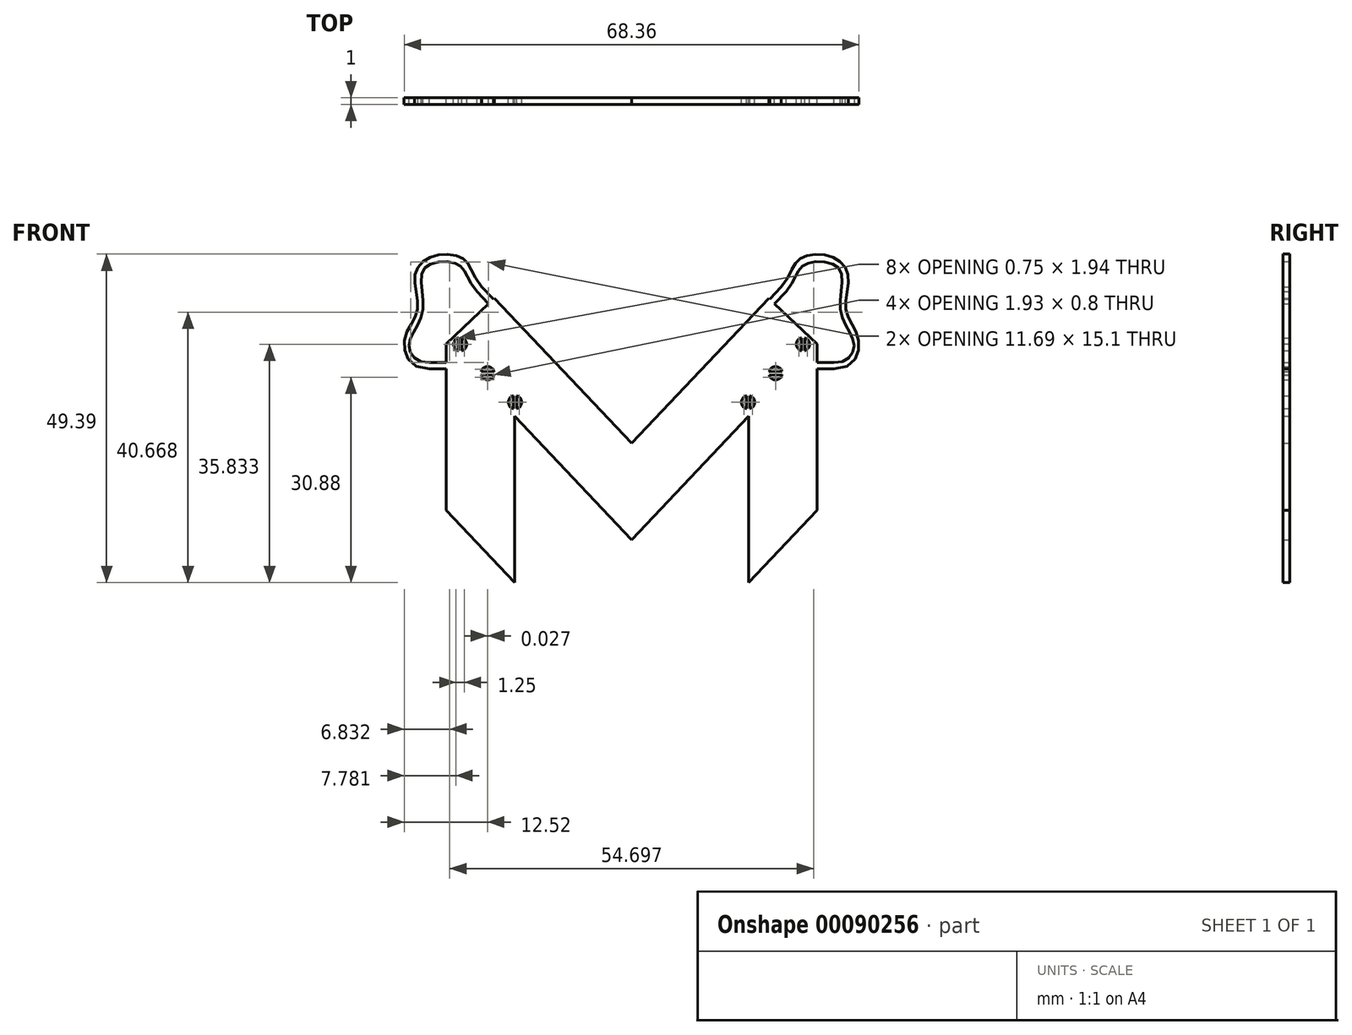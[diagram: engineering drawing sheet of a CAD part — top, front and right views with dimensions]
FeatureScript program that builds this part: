
annotation { "Feature Type Name" : "Feature", "Feature Type Description" : "" }
export const myFeature = defineFeature(function(context is Context, id is Id, definition is map)
    precondition{}
    {
        {
            var Q0;
            Q0=qCreatedBy(makeId("Front.planeOp"),FACE);
            var sketch = newSketch(context, id + "F0", { "sketchPlane" : qUnion([Q0])});
            skLineSegment(sketch, "E0", {"start": v(-27.9, 25) * mm, "end": v(0, -4.43) * mm});
            skLineSegment(sketch, "E1", {"start": v(0, -4.43) * mm, "end": v(27.9, 25) * mm});
            skLineSegment(sketch, "E2", {"start": v(27.9, 25) * mm, "end": v(20.64, 31.88) * mm});
            skLineSegment(sketch, "E3", {"start": v(20.64, 31.88) * mm, "end": v(0, 10.1) * mm});
            skLineSegment(sketch, "E4", {"start": v(-27.9, 25) * mm, "end": v(-20.64, 31.88) * mm});
            skLineSegment(sketch, "E5", {"start": v(-20.64, 31.88) * mm, "end": v(0, 10.1) * mm});
            skLineSegment(sketch, "E6", {"start": v(-27.9, 25) * mm, "end": v(-27.9, 0) * mm});
            skLineSegment(sketch, "E7", {"start": v(-27.9, 0) * mm, "end": v(-17.58, -10.89) * mm});
            skLineSegment(sketch, "E8", {"start": v(-17.58, -10.89) * mm, "end": v(-17.58, 14.11) * mm});
            skLineSegment(sketch, "E9.MirrorCS", {"start": v(17.58, -10.89) * mm, "end": v(17.58, 14.11) * mm});
            skLineSegment(sketch, "E10.MirrorCS", {"start": v(27.9, 25) * mm, "end": v(27.9, 0) * mm});
            skLineSegment(sketch, "E11.MirrorCS", {"start": v(27.9, 0) * mm, "end": v(17.58, -10.89) * mm});
            skLineSegment(sketch, "E12", {"start": v(-27.9, 22.23) * mm, "end": v(-30.4, 22.23) * mm});
            skLineSegment(sketch, "E13", {"start": v(-30.4, 22.23) * mm, "end": v(-30.4, 21.23) * mm});
            skLineSegment(sketch, "E14", {"start": v(-30.4, 21.23) * mm, "end": v(-27.9, 21.23) * mm});
            skLineSegment(sketch, "E15", {"start": v(-21.5, 31.06) * mm, "end": v(-23.22, 32.87) * mm});
            skLineSegment(sketch, "E16", {"start": v(-23.22, 32.87) * mm, "end": v(-22.5, 33.56) * mm});
            skLineSegment(sketch, "E17", {"start": v(-22.5, 33.56) * mm, "end": v(-20.78, 31.74) * mm});
            skFitSpline(sketch, "E18", {"points": [v(-30.4, 22.23) * mm, v(-33.44, 24.8) * mm, v(-31.4, 29.9) * mm, v(-31.16, 36.34) * mm, v(-26.06, 36.93) * mm, v(-23.22, 32.87) * mm], "startDerivative": vector(-33.33, -4.79) * mm, "endDerivative": vector(25.37, -29.65) * mm});
            skFitSpline(sketch, "E19", {"points": [v(-30.4, 21.23) * mm, v(-34.08, 25.8) * mm, v(-32.2, 30.15) * mm, v(-32.55, 35.35) * mm, v(-29.82, 38.22) * mm, v(-25.22, 37.77) * mm, v(-22.5, 33.56) * mm], "startDerivative": vector(-55.41, 0.59) * mm, "endDerivative": vector(28.93, -34.98) * mm});
            skCircle(sketch, "E20", {"center": v(-25.77, 24.94) * mm, "radius": 1 * mm});
            skCircle(sketch, "E21", {"center": v(-21.65, 20.59) * mm, "radius": 1 * mm});
            skCircle(sketch, "E22", {"center": v(-17.52, 16.23) * mm, "radius": 1 * mm});
            skLineSegment(sketch, "E23", {"start": v(-17.58, 14.11) * mm, "end": v(-10.32, 21) * mm, "construction": true});
            skLineSegment(sketch, "E24", {"start": v(-26.02, 25.91) * mm, "end": v(-26.02, 23.97) * mm});
            skLineSegment(sketch, "E25", {"start": v(-25.52, 23.97) * mm, "end": v(-25.52, 25.91) * mm});
            skLineSegment(sketch, "E26", {"start": v(-24.8, 21.73) * mm, "end": v(-17.54, 28.61) * mm, "construction": true});
            skLineSegment(sketch, "E27", {"start": v(-20.67, 17.38) * mm, "end": v(-13.41, 24.26) * mm, "construction": true});
            skLineSegment(sketch, "E28.MirrorCS", {"start": v(-22.6, 20.89) * mm, "end": v(-20.67, 20.79) * mm});
            skLineSegment(sketch, "E29.MirrorCS", {"start": v(-20.7, 20.29) * mm, "end": v(-22.63, 20.4) * mm});
            skLineSegment(sketch, "E30.MirrorCS", {"start": v(-17.77, 17.2) * mm, "end": v(-17.77, 15.27) * mm});
            skLineSegment(sketch, "E31.MirrorCS", {"start": v(-17.27, 15.27) * mm, "end": v(-17.27, 17.2) * mm});
            skLineSegment(sketch, "E32.MirrorCS", {"start": v(30.4, 21.23) * mm, "end": v(27.9, 21.23) * mm});
            skLineSegment(sketch, "E33.MirrorCS", {"start": v(27.9, 22.23) * mm, "end": v(30.4, 22.23) * mm});
            skLineSegment(sketch, "E34.MirrorCS", {"start": v(30.4, 22.23) * mm, "end": v(30.4, 21.23) * mm});
            skFitSpline(sketch, "E35.MirrorCS", {"points": [v(30.4, 22.23) * mm, v(33.44, 24.8) * mm, v(31.4, 29.9) * mm, v(31.16, 36.34) * mm, v(26.06, 36.93) * mm, v(23.22, 32.87) * mm], "startDerivative": vector(33.33, -4.79) * mm, "endDerivative": vector(-25.37, -29.65) * mm});
            skFitSpline(sketch, "E36.MirrorCS", {"points": [v(30.4, 21.23) * mm, v(34.08, 25.8) * mm, v(32.2, 30.15) * mm, v(32.55, 35.35) * mm, v(29.82, 38.22) * mm, v(25.22, 37.77) * mm, v(22.5, 33.56) * mm], "startDerivative": vector(55.41, 0.59) * mm, "endDerivative": vector(-28.93, -34.98) * mm});
            skLineSegment(sketch, "E37.MirrorCS", {"start": v(21.5, 31.06) * mm, "end": v(23.22, 32.87) * mm});
            skLineSegment(sketch, "E38.MirrorCS", {"start": v(23.22, 32.87) * mm, "end": v(22.5, 33.56) * mm});
            skLineSegment(sketch, "E39.MirrorCS", {"start": v(22.5, 33.56) * mm, "end": v(20.78, 31.74) * mm});
            skLineSegment(sketch, "E40.MirrorCS", {"start": v(26.02, 25.91) * mm, "end": v(26.02, 23.97) * mm});
            skLineSegment(sketch, "E41.MirrorCS", {"start": v(25.52, 23.97) * mm, "end": v(25.52, 25.91) * mm});
            skCircle(sketch, "E42.MirrorC", {"center": v(25.77, 24.94) * mm, "radius": 1 * mm});
            skCircle(sketch, "E43.MirrorC", {"center": v(21.65, 20.59) * mm, "radius": 1 * mm});
            skLineSegment(sketch, "E44.MirrorCS", {"start": v(22.6, 20.89) * mm, "end": v(20.67, 20.79) * mm});
            skLineSegment(sketch, "E45.MirrorCS", {"start": v(20.7, 20.29) * mm, "end": v(22.63, 20.4) * mm});
            skCircle(sketch, "E46.MirrorC", {"center": v(17.52, 16.23) * mm, "radius": 1 * mm});
            skLineSegment(sketch, "E47.MirrorCS", {"start": v(17.27, 15.27) * mm, "end": v(17.27, 17.2) * mm});
            skLineSegment(sketch, "E48.MirrorCS", {"start": v(17.77, 17.2) * mm, "end": v(17.77, 15.27) * mm});
            skSolve(sketch);
        }
        {
            var Q0;
            {var subQ48=sQuery(id+"F0.wireOp",EDGE,"E3");Q0=makeQuery(id+"F0.imprint","IMPRINT",FACE,{"disambiguationData":[TD([[makeQuery(id+"F0.imprint","IMPRINT",EDGE,{"derivedFrom":subQ48}),1.0]])]});}
            var Q1;
            {var subQ0=sQuery(id+"F0.wireOp",EDGE,"E28.MirrorCS");Q1=makeQuery(id+"F0.imprint","IMPRINT",FACE,{"disambiguationData":[TD([[makeQuery(id+"F0.imprint","IMPRINT",EDGE,{"derivedFrom":subQ0}),-1.0]])]});}
            var Q2;
            {var subQ0=sQuery(id+"F0.wireOp",EDGE,"E30.MirrorCS");Q2=makeQuery(id+"F0.imprint","IMPRINT",FACE,{"disambiguationData":[TD([[makeQuery(id+"F0.imprint","IMPRINT",EDGE,{"derivedFrom":subQ0}),1.0]])]});}
            var Q3;
            {var subQ0=sQuery(id+"F0.wireOp",EDGE,"E24");Q3=makeQuery(id+"F0.imprint","IMPRINT",FACE,{"disambiguationData":[TD([[makeQuery(id+"F0.imprint","IMPRINT",EDGE,{"derivedFrom":subQ0}),1.0]])]});}
            var Q4;
            {var subQ0=sQuery(id+"F0.wireOp",EDGE,"E47.MirrorCS");Q4=makeQuery(id+"F0.imprint","IMPRINT",FACE,{"disambiguationData":[TD([[makeQuery(id+"F0.imprint","IMPRINT",EDGE,{"derivedFrom":subQ0}),-1.0]])]});}
            var Q5;
            {var subQ0=sQuery(id+"F0.wireOp",EDGE,"E44.MirrorCS");Q5=makeQuery(id+"F0.imprint","IMPRINT",FACE,{"disambiguationData":[TD([[makeQuery(id+"F0.imprint","IMPRINT",EDGE,{"derivedFrom":subQ0}),1.0]])]});}
            var Q6;
            {var subQ0=sQuery(id+"F0.wireOp",EDGE,"E40.MirrorCS");Q6=makeQuery(id+"F0.imprint","IMPRINT",FACE,{"disambiguationData":[TD([[makeQuery(id+"F0.imprint","IMPRINT",EDGE,{"derivedFrom":subQ0}),-1.0]])]});}
            var Q7;
            Q7=makeQuery(id+"F0.imprint","IMPRINT",FACE,{"disambiguationData":[TD([[makeQuery(id+"F0.imprint","IMPRINT",EDGE,{"derivedFrom":sQuery(id+"F0.wireOp",EDGE,"E13")}),-1.0]])]});
            var Q8;
            {var subQ0=sQuery(id+"F0.wireOp",EDGE,"E15");Q8=makeQuery(id+"F0.imprint","IMPRINT",FACE,{"disambiguationData":[TD([[makeQuery(id+"F0.imprint","IMPRINT",EDGE,{"derivedFrom":subQ0}),-1.0]])]});}
            var Q9;
            {var subQ0=sQuery(id+"F0.wireOp",EDGE,"E12");Q9=makeQuery(id+"F0.imprint","IMPRINT",FACE,{"disambiguationData":[TD([[makeQuery(id+"F0.imprint","IMPRINT",EDGE,{"derivedFrom":subQ0}),1.0]])]});}
            var Q10;
            {var subQ0=sQuery(id+"F0.wireOp",EDGE,"E7");Q10=makeQuery(id+"F0.imprint","IMPRINT",FACE,{"disambiguationData":[TD([[makeQuery(id+"F0.imprint","IMPRINT",EDGE,{"derivedFrom":subQ0}),1.0]])]});}
            var Q11;
            {var subQ5=sQuery(id+"F0.wireOp",EDGE,"E9.MirrorCS");Q11=makeQuery(id+"F0.imprint","IMPRINT",FACE,{"disambiguationData":[TD([[makeQuery(id+"F0.imprint","IMPRINT",EDGE,{"derivedFrom":subQ5}),-1.0]])]});}
            var Q12;
            Q12=makeQuery(id+"F0.imprint","IMPRINT",FACE,{"disambiguationData":[TD([[makeQuery(id+"F0.imprint","IMPRINT",EDGE,{"derivedFrom":sQuery(id+"F0.wireOp",EDGE,"E34.MirrorCS")}),1.0]])]});
            var Q13;
            {var subQ0=sQuery(id+"F0.wireOp",EDGE,"E32.MirrorCS");Q13=makeQuery(id+"F0.imprint","IMPRINT",FACE,{"disambiguationData":[TD([[makeQuery(id+"F0.imprint","IMPRINT",EDGE,{"derivedFrom":subQ0}),-1.0]])]});}
            var Q14;
            {var subQ0=sQuery(id+"F0.wireOp",EDGE,"E37.MirrorCS");Q14=makeQuery(id+"F0.imprint","IMPRINT",FACE,{"disambiguationData":[TD([[makeQuery(id+"F0.imprint","IMPRINT",EDGE,{"derivedFrom":subQ0}),1.0]])]});}
            extrude(context, id + "F1", {"entities" : qUnion([Q0, Q1, Q2, Q3, Q4, Q5, Q6, Q7, Q8, Q9, Q10, Q11, Q12, Q13, Q14]), "depth" : 1 * mm});
        }
    });
